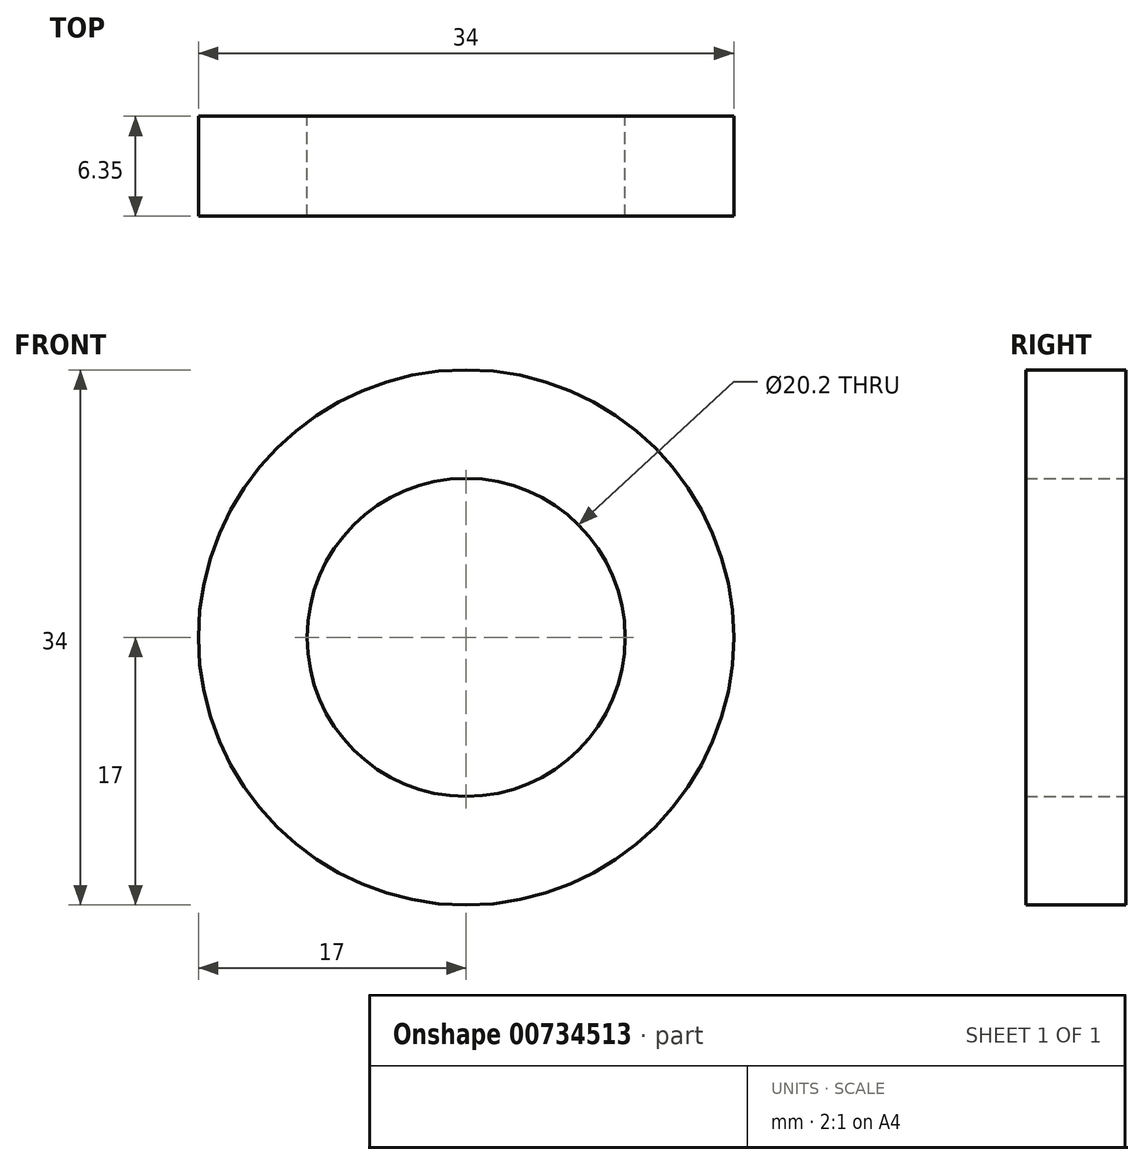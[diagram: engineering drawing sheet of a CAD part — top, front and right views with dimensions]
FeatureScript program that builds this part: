
annotation { "Feature Type Name" : "Feature", "Feature Type Description" : "" }
export const myFeature = defineFeature(function(context is Context, id is Id, definition is map)
    precondition{}
    {
        {
            var Q0;
            Q0=qCreatedBy(makeId("Front.planeOp"),FACE);
            var sketch = newSketch(context, id + "F0", { "sketchPlane" : qUnion([Q0])});
            skCircle(sketch, "E0", {"center": v(0, 0) * mm, "radius": 10.1 * mm});
            skCircle(sketch, "E1", {"center": v(0, 0) * mm, "radius": 17 * mm});
            skSolve(sketch);
        }
        {
            var Q0;
            Q0 = qSketchRegion(id + "F0", true);
            extrude(context, id + "F1", {"entities" : qUnion([Q0]), "depth" : 6.35 * mm, "offsetDistance" : 25.4 * mm});
        }
    });
